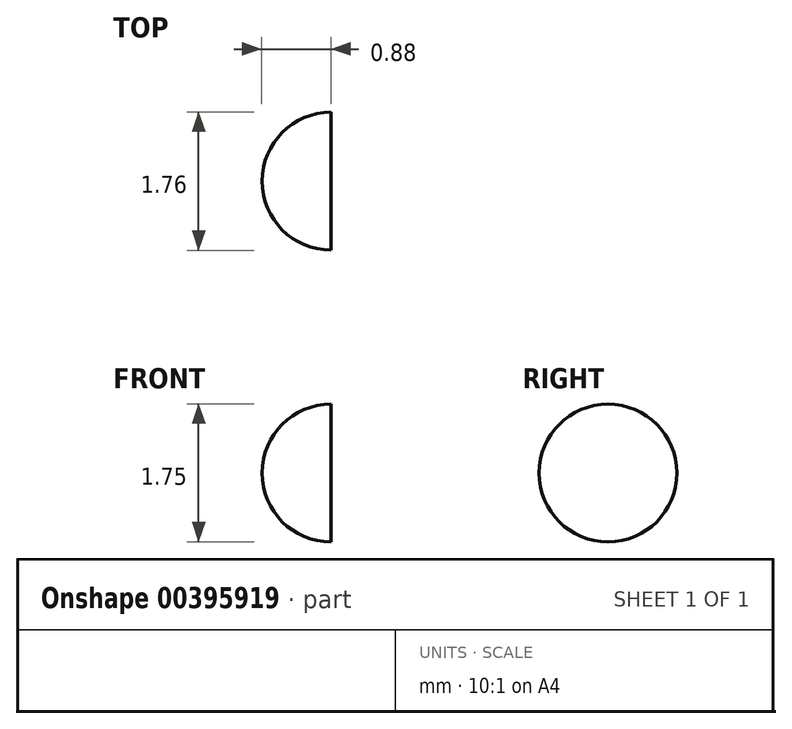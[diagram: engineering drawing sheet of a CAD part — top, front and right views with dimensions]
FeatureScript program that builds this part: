
annotation { "Feature Type Name" : "Feature", "Feature Type Description" : "" }
export const myFeature = defineFeature(function(context is Context, id is Id, definition is map)
    precondition{}
    {
        {
            var Q0;
            Q0=qCreatedBy(makeId("Front.planeOp"),FACE);
            var sketch = newSketch(context, id + "F0", { "sketchPlane" : qUnion([Q0])});
            skArc(sketch, "E0", {"start": v(0, 9.97) * mm, "mid": v(-0.88, 9.1) * mm, "end": v(0, 8.22) * mm});
            skArc(sketch, "E1", {"start": v(-0.14, 7.56) * mm, "mid": v(-1.03, 6.69) * mm, "end": v(-0.14, 5.81) * mm});
            skArc(sketch, "E2", {"start": v(0, 5.33) * mm, "mid": v(-0.78, 4.42) * mm, "end": v(0.1, 3.59) * mm});
            skArc(sketch, "E3", {"start": v(-0.14, 3.46) * mm, "mid": v(-1.01, 2.6) * mm, "end": v(-0.14, 1.71) * mm});
            skArc(sketch, "E4", {"start": v(0.27, 1.59) * mm, "mid": v(-0.6, 0.71) * mm, "end": v(0.27, -0.16) * mm});
            skLineSegment(sketch, "E5", {"start": v(0, 9.97) * mm, "end": v(0, 8.22) * mm});
            skLineSegment(sketch, "E6", {"start": v(-0.14, 7.56) * mm, "end": v(-0.14, 5.81) * mm});
            skLineSegment(sketch, "E7", {"start": v(0, 5.33) * mm, "end": v(0.1, 3.59) * mm});
            skLineSegment(sketch, "E8", {"start": v(-0.14, 3.46) * mm, "end": v(-0.14, 1.71) * mm});
            skLineSegment(sketch, "E9", {"start": v(0.27, 1.59) * mm, "end": v(0.27, -0.16) * mm});
            skSolve(sketch);
        }
        {
            var Q0;
            Q0=makeQuery(id+"F0.imprint","IMPRINT",FACE,{"disambiguationData":[TD([[makeQuery(id+"F0.imprint","IMPRINT",EDGE,{"derivedFrom":sQuery(id+"F0.wireOp",EDGE,"E0")}),1.0]])]});
            var Q1;
            Q1=sQuery(id+"F0.wireOp",EDGE,"E5");
            revolve(context, id + "F1", {"entities" : qUnion([Q0]), "axis" : qUnion([Q1]), "revolveType" : RevolveType.SYMMETRIC, "angle" : 180 * degree});
        }
    });
